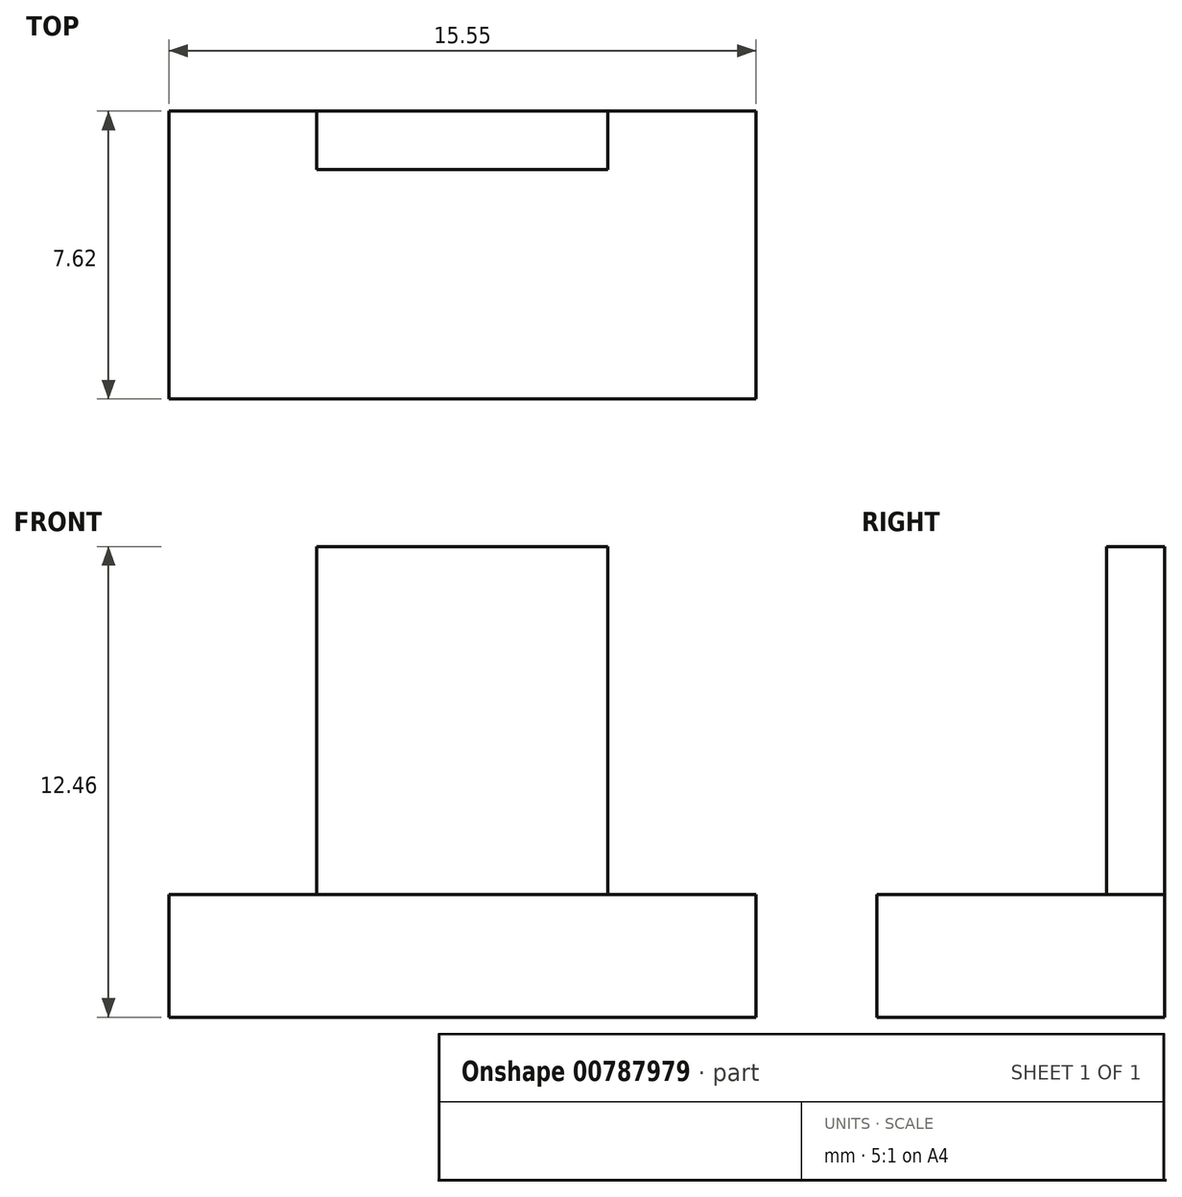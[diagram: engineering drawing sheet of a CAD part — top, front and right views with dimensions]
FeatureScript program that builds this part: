
annotation { "Feature Type Name" : "Feature", "Feature Type Description" : "" }
export const myFeature = defineFeature(function(context is Context, id is Id, definition is map)
    precondition{}
    {
        {
            var Q0;
            Q0=qCreatedBy(makeId("Top.planeOp"),FACE);
            var sketch = newSketch(context, id + "F0", { "sketchPlane" : qUnion([Q0])});
            skLineSegment(sketch, "E0", {"start": v(-66.14, 47) * mm, "end": v(-66.14, 39.39) * mm});
            skLineSegment(sketch, "E1", {"start": v(-66.14, 47) * mm, "end": v(-50.6, 47) * mm});
            skLineSegment(sketch, "E2", {"start": v(-50.6, 47) * mm, "end": v(-50.6, 39.39) * mm});
            skLineSegment(sketch, "E3", {"start": v(-50.6, 39.39) * mm, "end": v(-66.14, 39.39) * mm});
            skSolve(sketch);
        }
        {
            var Q0;
            Q0 = qSketchRegion(id + "F0", true);
            extrude(context, id + "F1", {"entities" : qUnion([Q0]), "depth" : 3.24 * mm, "offsetDistance" : 25 * mm});
        }
        {
            var Q0;
            Q0=makeQuery(id+"F1.opExtrude","CAP_FACE",FACE,{"disambiguationData":[OSD([sQuery(id+"F0.wireOp",EDGE,"E0"),sQuery(id+"F0.wireOp",EDGE,"E1"),sQuery(id+"F0.wireOp",EDGE,"E2"),sQuery(id+"F0.wireOp",EDGE,"E3")])],"isStart":false});
            var sketch = newSketch(context, id + "F2", { "sketchPlane" : qUnion([Q0])});
            skLineSegment(sketch, "E4", {"start": v(-62.22, 47) * mm, "end": v(-62.22, 45.47) * mm});
            skLineSegment(sketch, "E5", {"start": v(-54.51, 47) * mm, "end": v(-54.51, 45.47) * mm});
            skLineSegment(sketch, "E6", {"start": v(-62.22, 45.47) * mm, "end": v(-54.51, 45.47) * mm});
            skLineSegment(sketch, "E7", {"start": v(-62.22, 47) * mm, "end": v(-54.51, 47) * mm});
            skSolve(sketch);
        }
        {
            var Q0;
            Q0 = qSketchRegion(id + "F2", true);
            extrude(context, id + "F3", {"entities" : qUnion([Q0]), "operationType" : NewBodyOperationType.ADD, "depth" : 9.22 * mm, "offsetDistance" : 25 * mm});
        }
    });
